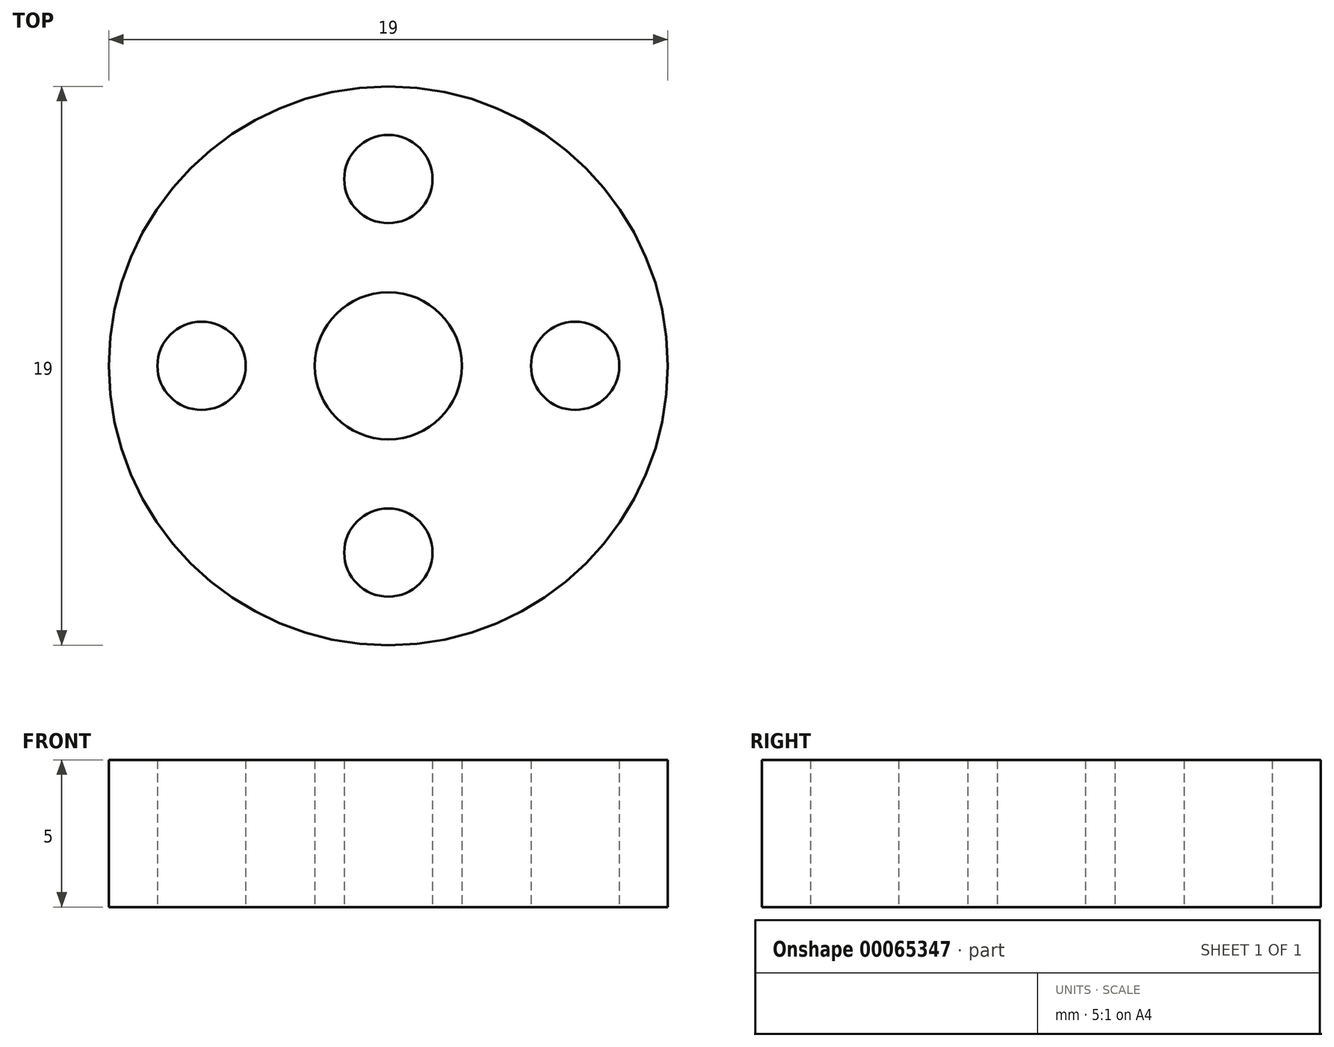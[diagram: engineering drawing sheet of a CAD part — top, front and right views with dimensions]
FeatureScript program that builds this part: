
annotation { "Feature Type Name" : "Feature", "Feature Type Description" : "" }
export const myFeature = defineFeature(function(context is Context, id is Id, definition is map)
    precondition{}
    {
        {
            var Q0;
            Q0=qCreatedBy(makeId("Top.planeOp"),FACE);
            var sketch = newSketch(context, id + "F0", { "sketchPlane" : qUnion([Q0])});
            skCircle(sketch, "E0", {"center": v(0, 0) * mm, "radius": 9.5 * mm});
            skCircle(sketch, "E1", {"center": v(0, 0) * mm, "radius": 2.5 * mm});
            skCircle(sketch, "E2", {"center": v(0, 6.35) * mm, "radius": 1.5 * mm});
            skCircle(sketch, "E3.1.0", {"center": v(-6.35, 0) * mm, "radius": 1.5 * mm});
            skCircle(sketch, "E3.2.0", {"center": v(0, -6.35) * mm, "radius": 1.5 * mm});
            skCircle(sketch, "E3.3.0", {"center": v(6.35, 0) * mm, "radius": 1.5 * mm});
            skSolve(sketch);
        }
        {
            var Q0;
            Q0 = qSketchRegion(id + "F0", true);
            extrude(context, id + "F1", {"entities" : qUnion([Q0]), "depth" : 5 * mm});
        }
    });
